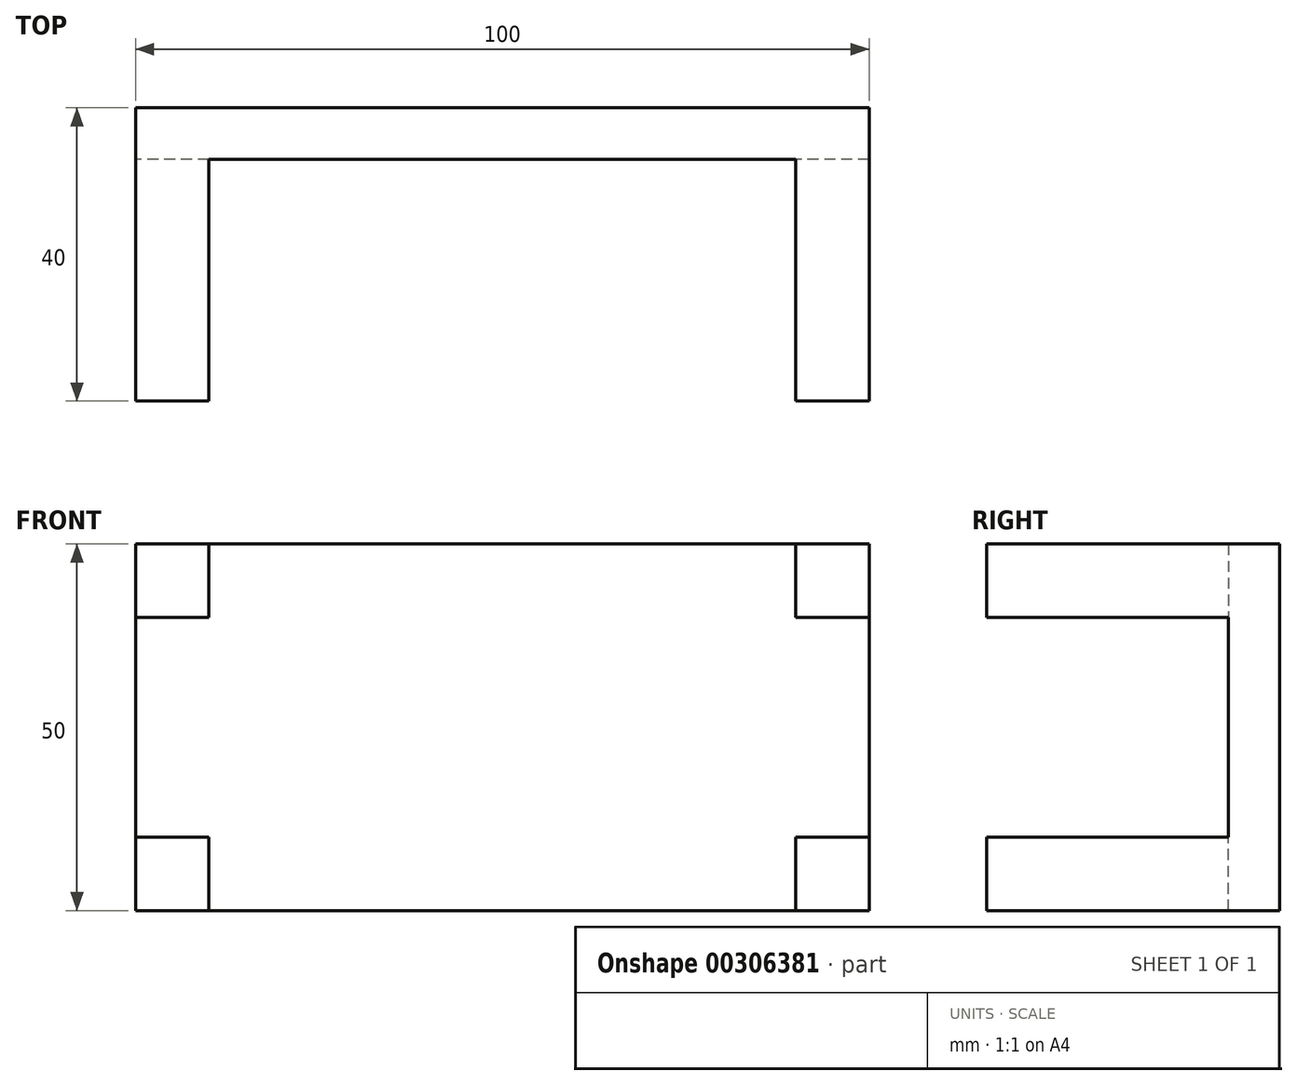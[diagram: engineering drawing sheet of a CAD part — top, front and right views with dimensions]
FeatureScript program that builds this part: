
annotation { "Feature Type Name" : "Feature", "Feature Type Description" : "" }
export const myFeature = defineFeature(function(context is Context, id is Id, definition is map)
    precondition{}
    {
        {
            var Q0;
            Q0=qCreatedBy(makeId("Front.planeOp"),FACE);
            var sketch = newSketch(context, id + "F0", { "sketchPlane" : qUnion([Q0])});
            skLineSegment(sketch, "E0.bottom", {"start": v(31.1, 0) * mm, "end": v(-68.9, 0) * mm});
            skLineSegment(sketch, "E0.top", {"start": v(31.1, 50) * mm, "end": v(-68.9, 50) * mm});
            skLineSegment(sketch, "E0.left", {"start": v(31.1, 0) * mm, "end": v(31.1, 50) * mm});
            skLineSegment(sketch, "E0.right", {"start": v(-68.9, 0) * mm, "end": v(-68.9, 50) * mm});
            skSolve(sketch);
        }
        {
            var Q0;
            Q0=makeQuery(id+"F0.imprint","IMPRINT",FACE,{"disambiguationData":[TD([[makeQuery(id+"F0.imprint","IMPRINT",EDGE,{"derivedFrom":sQuery(id+"F0.wireOp",EDGE,"E0.bottom")}),-1.0]])]});
            extrude(context, id + "F1", {"entities" : qUnion([Q0]), "depth" : 25 * mm});
        }
        {
            var Q0;
            Q0=makeQuery(id+"F1.opExtrude","CAP_FACE",FACE,{"disambiguationData":[OSD([sQuery(id+"F0.wireOp",EDGE,"E0.bottom"),sQuery(id+"F0.wireOp",EDGE,"E0.top"),sQuery(id+"F0.wireOp",EDGE,"E0.left"),sQuery(id+"F0.wireOp",EDGE,"E0.right")])],"isStart":false});
            var sketch = newSketch(context, id + "F2", { "sketchPlane" : qUnion([Q0])});
            skLineSegment(sketch, "E1", {"start": v(-68.9, 0) * mm, "end": v(-58.9, 0) * mm});
            skLineSegment(sketch, "E2", {"start": v(-58.9, 0) * mm, "end": v(-58.9, 10) * mm});
            skLineSegment(sketch, "E3", {"start": v(-58.9, 10) * mm, "end": v(-68.9, 10) * mm});
            skLineSegment(sketch, "E4", {"start": v(-68.9, 0) * mm, "end": v(-68.9, 10) * mm});
            skLineSegment(sketch, "E5", {"start": v(-68.9, 50) * mm, "end": v(-58.9, 50) * mm});
            skLineSegment(sketch, "E6", {"start": v(-58.9, 50) * mm, "end": v(-58.9, 40) * mm});
            skLineSegment(sketch, "E7", {"start": v(-58.9, 40) * mm, "end": v(-68.9, 40) * mm});
            skLineSegment(sketch, "E8", {"start": v(-68.9, 40) * mm, "end": v(-68.9, 50) * mm});
            skLineSegment(sketch, "E9", {"start": v(31.1, 50) * mm, "end": v(31.1, 40) * mm});
            skLineSegment(sketch, "E10", {"start": v(31.1, 40) * mm, "end": v(21.1, 40) * mm});
            skLineSegment(sketch, "E11", {"start": v(21.1, 40) * mm, "end": v(21.1, 50) * mm});
            skLineSegment(sketch, "E12", {"start": v(21.1, 50) * mm, "end": v(31.1, 50) * mm});
            skLineSegment(sketch, "E13", {"start": v(31.1, 0) * mm, "end": v(31.1, 10) * mm});
            skLineSegment(sketch, "E14", {"start": v(31.1, 10) * mm, "end": v(21.1, 10) * mm});
            skLineSegment(sketch, "E15", {"start": v(21.1, 10) * mm, "end": v(21.1, 0) * mm});
            skLineSegment(sketch, "E16", {"start": v(21.1, 0) * mm, "end": v(31.1, 0) * mm});
            skSolve(sketch);
        }
        {
            var Q0;
            Q0 = qSketchRegion(id + "F2", true);
            extrude(context, id + "F3", {"entities" : qUnion([Q0]), "operationType" : NewBodyOperationType.ADD, "depth" : 15 * mm});
        }
        {
            var Q0;
            Q0=makeQuery(id+"F1.opExtrude","CAP_FACE",FACE,{"disambiguationData":[OSD([sQuery(id+"F0.wireOp",EDGE,"E0.bottom"),sQuery(id+"F0.wireOp",EDGE,"E0.top"),sQuery(id+"F0.wireOp",EDGE,"E0.left"),sQuery(id+"F0.wireOp",EDGE,"E0.right")])],"isStart":false});
            extrude(context, id + "F4", {"entities" : qUnion([Q0]), "operationType" : NewBodyOperationType.REMOVE, "oppositeDirection" : true, "depth" : 18 * mm});
        }
    });
